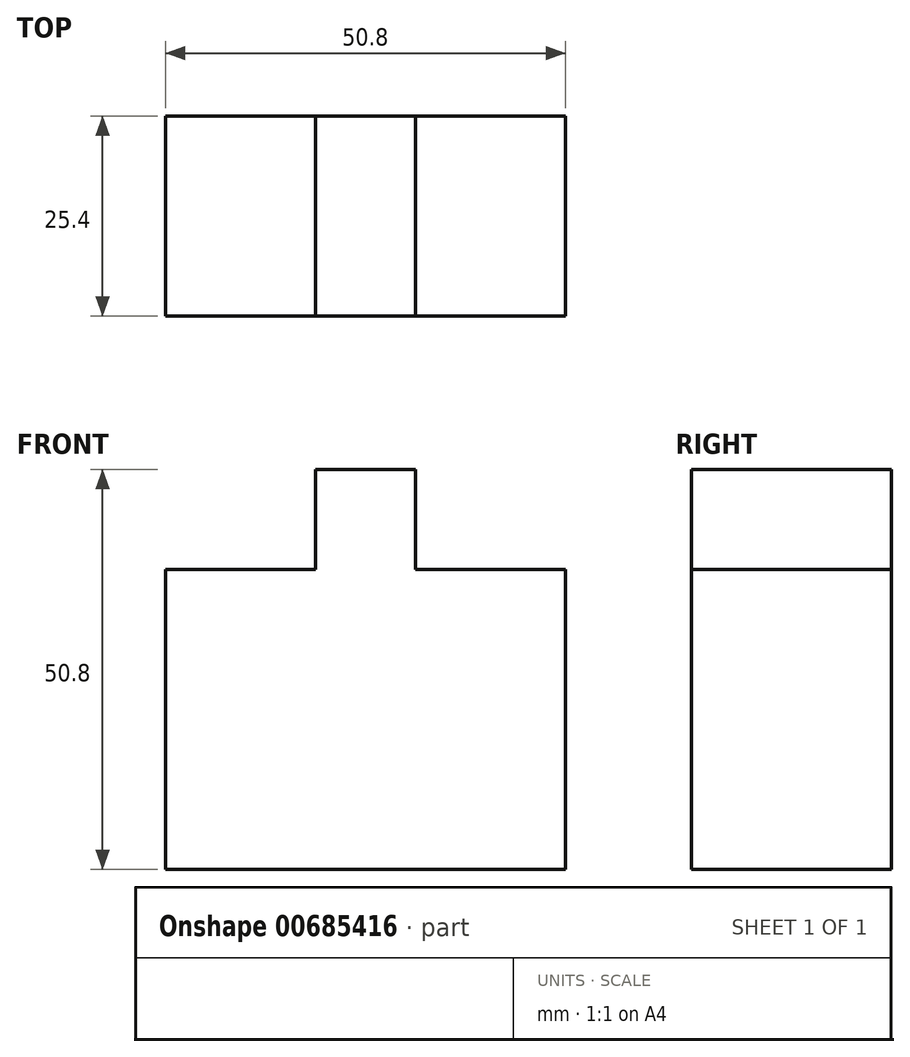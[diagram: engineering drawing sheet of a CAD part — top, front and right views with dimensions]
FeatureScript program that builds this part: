
annotation { "Feature Type Name" : "Feature", "Feature Type Description" : "" }
export const myFeature = defineFeature(function(context is Context, id is Id, definition is map)
    precondition{}
    {
        {
            var Q0;
            Q0=qCreatedBy(makeId("Front.planeOp"),FACE);
            var sketch = newSketch(context, id + "F0", { "sketchPlane" : qUnion([Q0])});
            skLineSegment(sketch, "E0", {"start": v(0, 0) * mm, "end": v(0, 38.1) * mm});
            skLineSegment(sketch, "E1", {"start": v(0, 38.1) * mm, "end": v(19.05, 38.1) * mm});
            skLineSegment(sketch, "E2", {"start": v(19.05, 38.1) * mm, "end": v(19.05, 50.8) * mm});
            skLineSegment(sketch, "E3", {"start": v(19.05, 50.8) * mm, "end": v(31.75, 50.8) * mm});
            skLineSegment(sketch, "E4", {"start": v(31.75, 50.8) * mm, "end": v(31.75, 38.1) * mm});
            skLineSegment(sketch, "E5", {"start": v(31.75, 38.1) * mm, "end": v(50.8, 38.1) * mm});
            skLineSegment(sketch, "E6", {"start": v(50.8, 38.1) * mm, "end": v(50.8, 0) * mm});
            skLineSegment(sketch, "E7", {"start": v(50.8, 0) * mm, "end": v(0, 0) * mm});
            skSolve(sketch);
        }
        {
            var Q0;
            Q0=makeQuery(id+"F0.imprint","IMPRINT",FACE,{"disambiguationData":[TD([[makeQuery(id+"F0.imprint","IMPRINT",EDGE,{"derivedFrom":sQuery(id+"F0.wireOp",EDGE,"E0")}),-1.0]])]});
            extrude(context, id + "F1", {"entities" : qUnion([Q0]), "depth" : 25.4 * mm, "offsetDistance" : 25.4 * mm});
        }
    });
